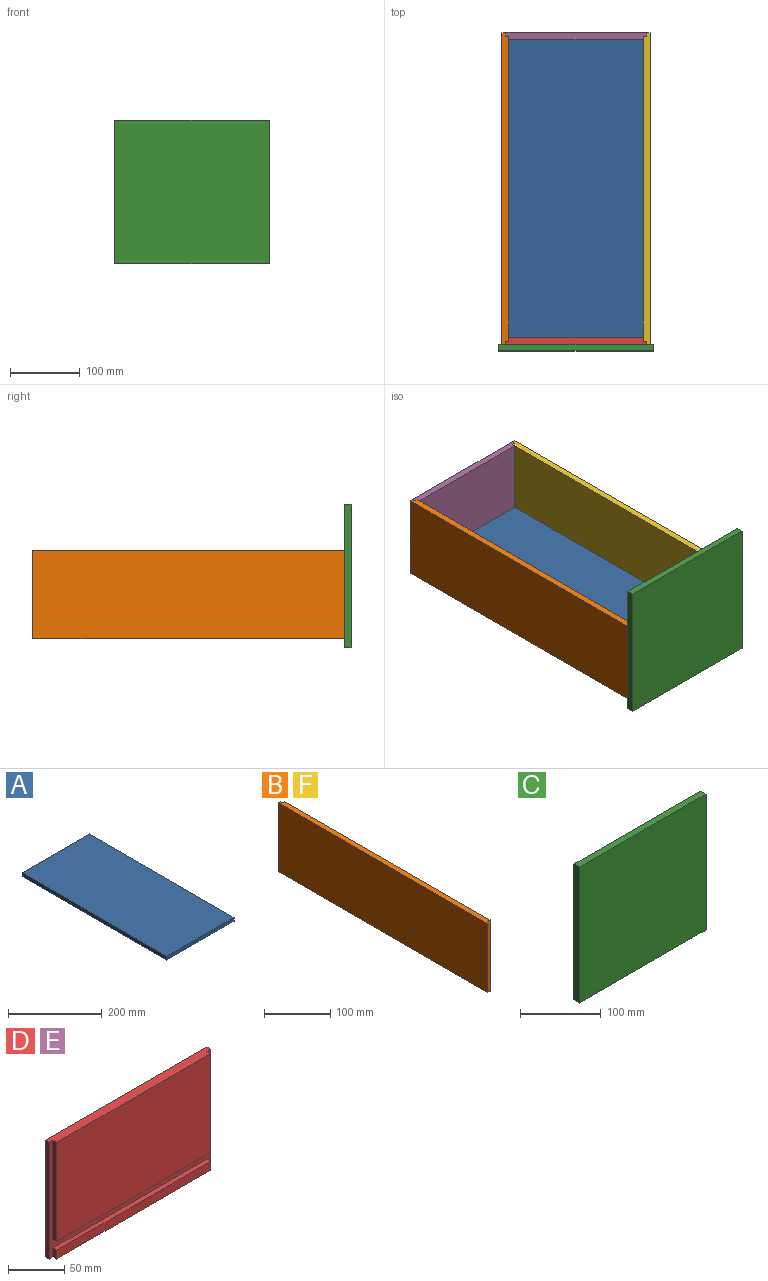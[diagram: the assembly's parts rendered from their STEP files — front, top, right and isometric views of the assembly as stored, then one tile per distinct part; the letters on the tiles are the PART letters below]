
ASSEMBLY  parts=6 mates=5
PART A: 6 faces, bbox 203.2x438.2x9.5 mm
  f0: plane 438.15x9.53mm, normal (-1,0,0), area 4173.4mm2, adj f1,f3,f4,f5
  f1: plane 203.2x9.53mm, normal (0,-1,0), area 1935.5mm2, adj f0,f2,f4,f5
  f2: plane 438.15x9.53mm, normal (1,0,0), area 4173.4mm2, adj f1,f3,f4,f5
  f3: plane 203.2x9.53mm, normal (0,1,0), area 1935.5mm2, adj f0,f2,f4,f5
  f4: plane 438.15x203.2mm, normal (0,0,1), area 89032.1mm2, adj f0,f1,f2,f3
  f5: plane 438.15x203.2mm, normal (0,0,-1), area 89032.1mm2, adj f0,f1,f2,f3
PART B: 14 faces, bbox 9.5x447.7x127 mm
  f0: plane 9.53x4.76mm, normal (0,-1,0), area 45.4mm2, adj f7,f8,f11,f12
  f1: plane 438.15x107.95mm, normal (1,0,0), area 47298.3mm2, adj f3,f6,f10,f13
  f2: plane 9.53x4.76mm, normal (0,1,0), area 45.4mm2, adj f7,f8,f11,f12
  f3: plane 107.95x4.76mm, normal (0,1,0), area 514.1mm2, adj f1,f8,f10,f13
  f4: plane 447.68x127mm, normal (-1,0,0), area 56854.7mm2, adj f5,f9,f10,f11
  f5: plane 127x4.76mm, normal (0,-1,0), area 604.8mm2, adj f4,f8,f10,f11
  f6: plane 107.95x4.76mm, normal (0,-1,0), area 514.1mm2, adj f1,f8,f10,f13
  f7: plane 438.15x9.53mm, normal (1,0,0), area 4173.4mm2, adj f0,f2,f11,f12
  f8: plane 447.68x127mm, normal (1,0,0), area 5383.1mm2, adj f0,f2,f3,f5,f6,f9,f10,f11
  f9: plane 127x4.76mm, normal (0,1,0), area 604.8mm2, adj f4,f8,f10,f11
  f10: plane 447.68x9.53mm, normal (0,0,1), area 4218.7mm2, adj f1,f3,f4,f5,f6,f8,f9
  f11: plane 447.68x9.53mm, normal (0,0,-1), area 4218.7mm2, adj f0,f2,f4,f5,f7,f8,f9
  f12: plane 438.15x4.76mm, normal (0,0,1), area 2086.7mm2, adj f0,f2,f7,f8
  f13: plane 438.15x4.76mm, normal (0,0,-1), area 2086.7mm2, adj f1,f3,f6,f8
PART C: 6 faces, bbox 222.3x9.5x206.4 mm
  f0: plane 222.25x206.38mm, normal (0,1,0), area 45866.8mm2, adj f1,f3,f4,f5
  f1: plane 206.38x9.53mm, normal (-1,0,0), area 1965.7mm2, adj f0,f2,f4,f5
  f2: plane 222.25x206.38mm, normal (0,-1,0), area 45866.8mm2, adj f1,f3,f4,f5
  f3: plane 206.38x9.53mm, normal (1,0,0), area 1965.7mm2, adj f0,f2,f4,f5
  f4: plane 222.25x9.53mm, normal (0,0,1), area 2116.9mm2, adj f0,f1,f2,f3
  f5: plane 222.25x9.53mm, normal (0,0,-1), area 2116.9mm2, adj f0,f1,f2,f3
PART D: 14 faces, bbox 203.2x9.5x127 mm
  f0: plane 193.68x9.53mm, normal (0,-1,0), area 1844.8mm2, adj f1,f2,f11,f12
  f1: plane 9.53x4.76mm, normal (1,0,0), area 45.4mm2, adj f0,f8,f11,f12
  f2: plane 9.53x4.76mm, normal (-1,0,0), area 45.4mm2, adj f0,f8,f11,f12
  f3: plane 203.2x127mm, normal (0,1,0), area 25806.4mm2, adj f4,f9,f10,f11
  f4: plane 127x4.76mm, normal (-1,0,0), area 604.8mm2, adj f3,f8,f10,f11
  f5: plane 107.95x4.76mm, normal (-1,0,0), area 514.1mm2, adj f6,f8,f10,f13
  f6: plane 193.68x107.95mm, normal (0,-1,0), area 20907.2mm2, adj f5,f7,f10,f13
  f7: plane 107.95x4.76mm, normal (1,0,0), area 514.1mm2, adj f6,f8,f10,f13
  f8: plane 203.2x127mm, normal (0,-1,0), area 3054.4mm2, adj f1,f2,f4,f5,f7,f9,f10,f11
  f9: plane 127x4.76mm, normal (1,0,0), area 604.8mm2, adj f3,f8,f10,f11
  f10: plane 203.2x9.53mm, normal (0,0,1), area 1890.1mm2, adj f3,f4,f5,f6,f7,f8,f9
  f11: plane 203.2x9.53mm, normal (0,0,-1), area 1890.1mm2, adj f0,f1,f2,f3,f4,f8,f9
  f12: plane 193.68x4.76mm, normal (0,0,1), area 922.4mm2, adj f0,f1,f2,f8
  f13: plane 193.68x4.76mm, normal (0,0,-1), area 922.4mm2, adj f5,f6,f7,f8
PART E: same geometry as D
PART F: same geometry as B
PLACE A t=(-182.13,-8.58,-51.07)mm
PLACE B t=(-80.53,-22.86,-60.6)mm
PLACE C t=(-80.53,-22.86,-60.6)mm fixed
PLACE D rot(axis=(0,0,1),180deg) t=(-80.53,443.86,-60.6)mm
PLACE E t=(-80.53,-22.86,-60.6)mm
PLACE F rot(axis=(0,0,1),180deg) t=(-80.53,443.86,-60.6)mm
MATE fastened D.f3 <-> C.f0  axis (0,-1,0) through (-80.53,-13.34,-60.6)mm
MATE fastened B.f10 <-> D.f10  axis (0,0,1) through (-182.13,-10.96,66.4)mm
MATE fastened A.f4 <-> D.f13  axis (0,0,1) through (-80.53,-8.58,-41.55)mm
MATE fastened F.f10 <-> D.f10  axis (0,0,1) through (21.07,-10.96,66.4)mm
MATE fastened E.f10 <-> B.f10  axis (0,0,1) through (-182.13,431.96,66.4)mm
